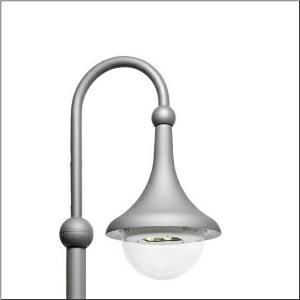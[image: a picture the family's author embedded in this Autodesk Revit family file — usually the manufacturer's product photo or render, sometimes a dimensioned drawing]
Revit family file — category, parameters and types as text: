
# Revit family: kleine_glocke_iq___st1_2a_5xa1575e1f108_8dd9
name_source: partatom
category: Lighting Fixtures
units: mm (PartAtom-declared; Revit-internal decimal feet)

## family parameters
Cut with Voids When Loaded = No
Host = Face
Light Source = No
Part Type = Normal
Room Calculation Point = No
Round Connector Dimension = Use Diameter
Shared = No

## types (1)
- --- (1 x LED, 3220 lm, 20.1 W, 3000K)
    Apparent Load = 20 VA
    CIE Flux Codes = 28 65 95 100 100
    Color Rendering = 70
    Color Temperature = 3000K
    Default Elevation = 1800 mm
    Description = Small Bell iQ, mast luminaire, primary light control with 3 zone facetted reflector, of plastic, silver coated, primary optical cover: enclosure, of PMMA, transparent, light distribution: ST1.2a, light emission: direct distribution, primary light characteristic: asymmetric, installation type: suspended mounting, LED, High Power LED, rated luminous flux: 3.220lm, luminous efficacy: 160lm/W, light colour: 730, colour temperature: 3000K, control gear: iQ Street-Remote, control: optimised constant luminous flux control (CLO 2.0), Desk-Remote (wireless, voltage-free reading and setting of iQ features in the workshop via application-optimized NFC function/RFID function), Light-Fading, Smart-Wire, Night-Set, Lumen-Switch, Temp-Guard, Auto-Match, Street-Remote, pre-setting: logarithmic dimming characteristic, mains connection: 230..240V, AC, 50/60Hz, start of lifetime: 20W, end of service life: 21W, reduction: 10W, luminaire housing, bell-shaped, of glass-fibre reinforced polyester, coated, Siteco® metallic grey (DB 702S), please order curved mast extension separately, diameter: 430mm, height: 575mm, mounting height: 2.5..4.0m, protection rating (complete): IP54, insulation class (complete): insulation class II (safety insulation), certification: CE, ENEC, VDE, impact resistance: IK09, standard-compliant lighting for roads and squares, packaging unit: 1 piece

Light Distribution: ST1.2a
    Height = 575 mm
    Lamp = 1 x LED
    Lamp Light Flux = 3220 lm
    Lamp Power = 20.1 W
    Lamp count = 1
    Length = 430 mm
    Luminous efficacy = 160 lm/W
    Manufacturer = Siteco
    ModVariant = No
    Model = 5XA1575E1F108
    Number of Poles = 1
    OnlyDefault = Yes
    Power Factor = 1
    Product Name = Kleine Glocke iQ | ST1.2a
    Product group = mast luminaire | pylon annexe
    ProductGroupID = 6201
    Protection Class = Protection class II
    Protection Degree = IP 54
    RLX_Detail_Level = 1
    RLX_Emergency_Light_Flux = 0 lm
    RLX_Emergency_Type = 0
    RLX_Emergency_Type_DB = No
    RlxData = <blob elided: 73401 chars, md5=8aaae614>
    Socket = socket
    Standby Power = 0 W
    System Light Flux = 3220 lm
    System Power = 20 W
    Type Comments = factory setting: luminous flux: 100 % | dim-lin: 254 | 376 mA
    Type Image = l_1347699.jpg
    URL = http://relux.com
    VarID = @adj_060044
    Voltage = 0 V
    Weight = 0.00 kg
    Width = 0 mm  [stored 0 ft]

note: [stored X ft] marks values corroborated as IEEE doubles in the binary element streams (Revit-internal decimal feet)

## geometry (parser evidence)
native form markers: Blend x4, Sweep x11
no freeform markers — native parametric forms only
